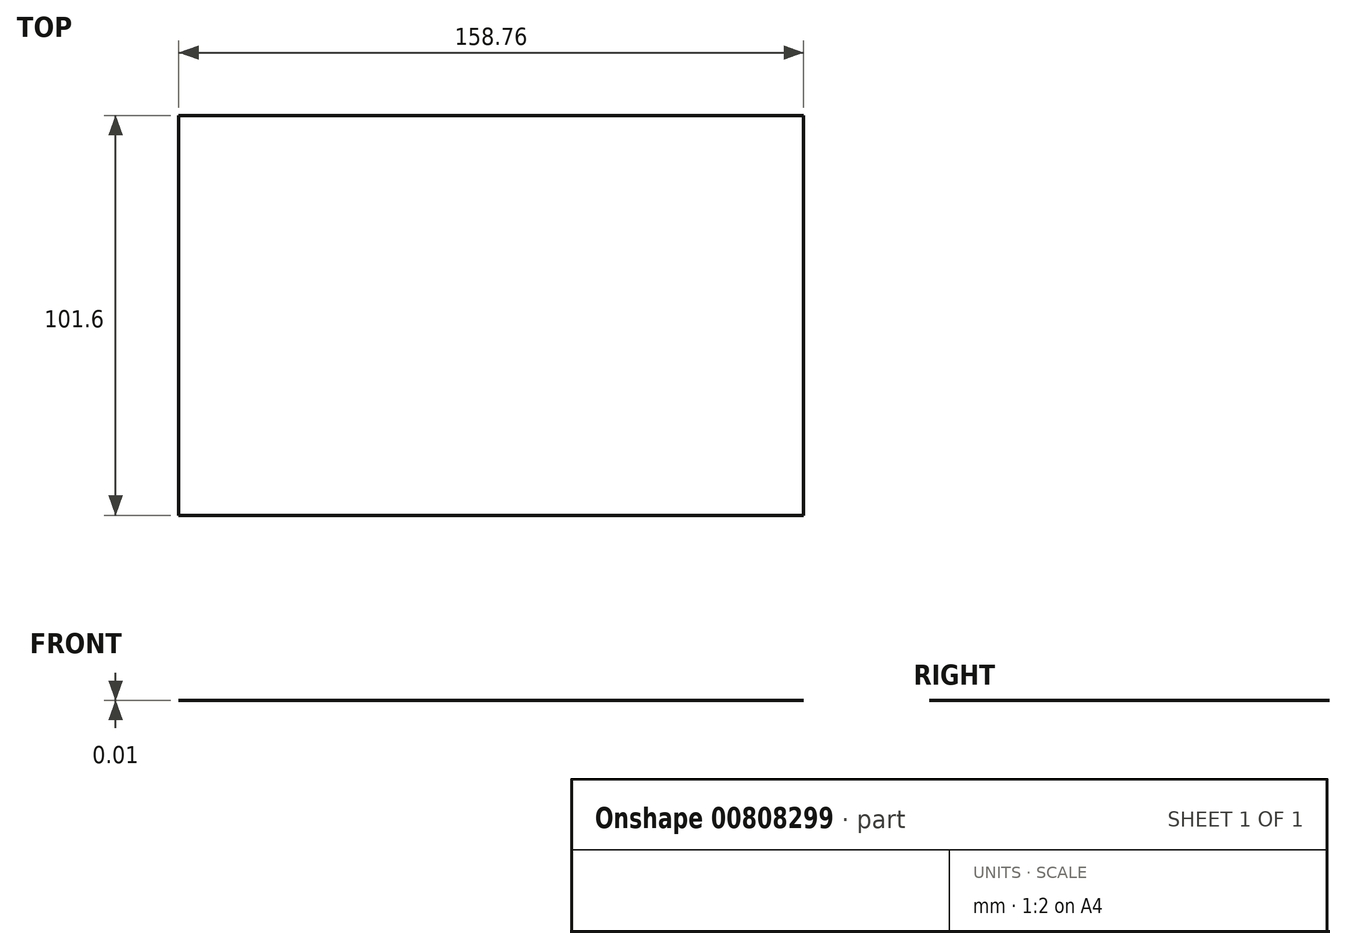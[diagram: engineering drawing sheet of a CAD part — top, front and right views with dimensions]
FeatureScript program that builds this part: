
annotation { "Feature Type Name" : "Feature", "Feature Type Description" : "" }
export const myFeature = defineFeature(function(context is Context, id is Id, definition is map)
    precondition{}
    {
        {
            var Q0;
            Q0=qCreatedBy(makeId("Top.planeOp"),FACE);
            var sketch = newSketch(context, id + "F0", { "sketchPlane" : qUnion([Q0])});
            skLineSegment(sketch, "E0.bottom", {"start": v(79.38, -50.8) * mm, "end": v(-79.37, -50.8) * mm});
            skLineSegment(sketch, "E0.top", {"start": v(79.37, 50.8) * mm, "end": v(-79.38, 50.8) * mm});
            skLineSegment(sketch, "E0.left", {"start": v(79.38, -50.8) * mm, "end": v(79.37, 50.8) * mm});
            skLineSegment(sketch, "E0.right", {"start": v(-79.37, -50.8) * mm, "end": v(-79.38, 50.8) * mm});
            skPoint(sketch, "E0.middle", {"position": v(0, 0) * mm});
            skSolve(sketch);
        }
        {
            var Q0;
            Q0=qSketchRegion(id+"F0",true);
            extrude(context, id + "F1", {"entities" : qUnion([Q0]), "depth" : 3 / 203.2 * mm, "offsetDistance" : 25 * mm});
        }
    });
